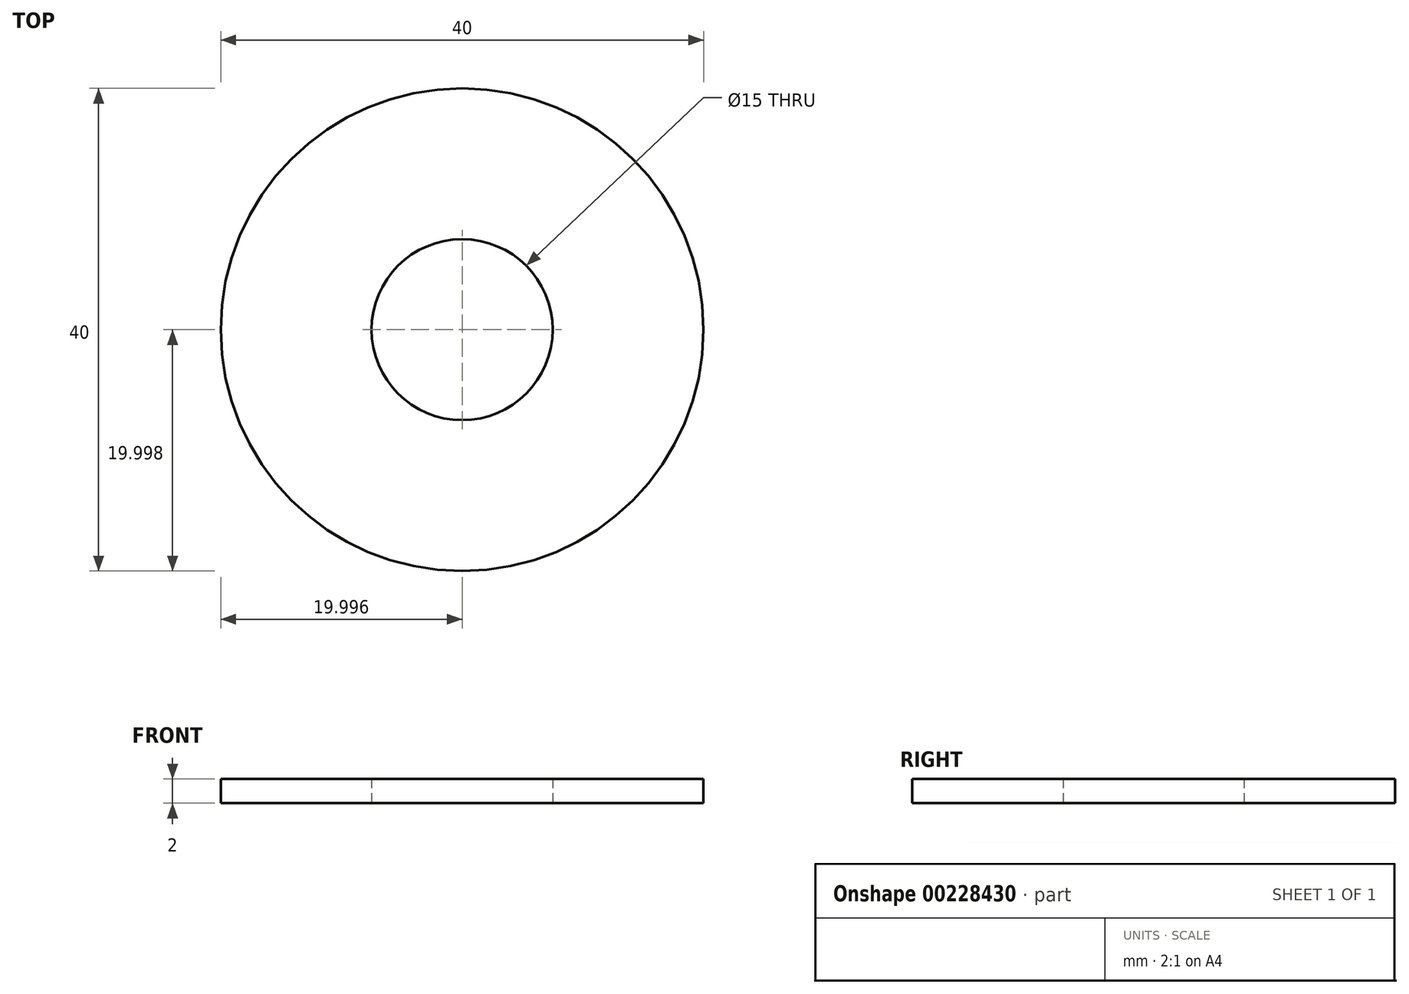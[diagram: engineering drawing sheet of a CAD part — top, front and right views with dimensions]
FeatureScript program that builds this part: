
annotation { "Feature Type Name" : "Feature", "Feature Type Description" : "" }
export const myFeature = defineFeature(function(context is Context, id is Id, definition is map)
    precondition{}
    {
        {
            var Q0;
            Q0=qCreatedBy(makeId("Top.planeOp"),FACE);
            var sketch = newSketch(context, id + "F0", { "sketchPlane" : qUnion([Q0])});
            skCircle(sketch, "E0", {"center": v(-6.03, 19.07) * mm, "radius": 20 * mm});
            skSolve(sketch);
        }
        {
            var Q0;
            Q0 = qSketchRegion(id + "F0", true);
            extrude(context, id + "F1", {"entities" : qUnion([Q0]), "depth" : 2 * mm});
        }
        {
            var Q0;
            Q0=sQuery(id+"F0.wireOp",VERTEX,"E0.center");
            var Q1;
            Q1=makeQuery(id+"F1.opExtrude","SWEPT_BODY",BODY,{"disambiguationData":[OSD([sQuery(id+"F0.wireOp",EDGE,"E0")])]});
            hole(context, id + "F2", {"style" : HoleStyle.SIMPLE, "endStyle" : HoleEndStyle.THROUGH, "oppositeDirection" : true, "holeDiameter" : 15 * mm, "locations" : qUnion([Q0]), "scope" : qUnion([Q1]), "isTappedThrough" : true});
        }
    });
